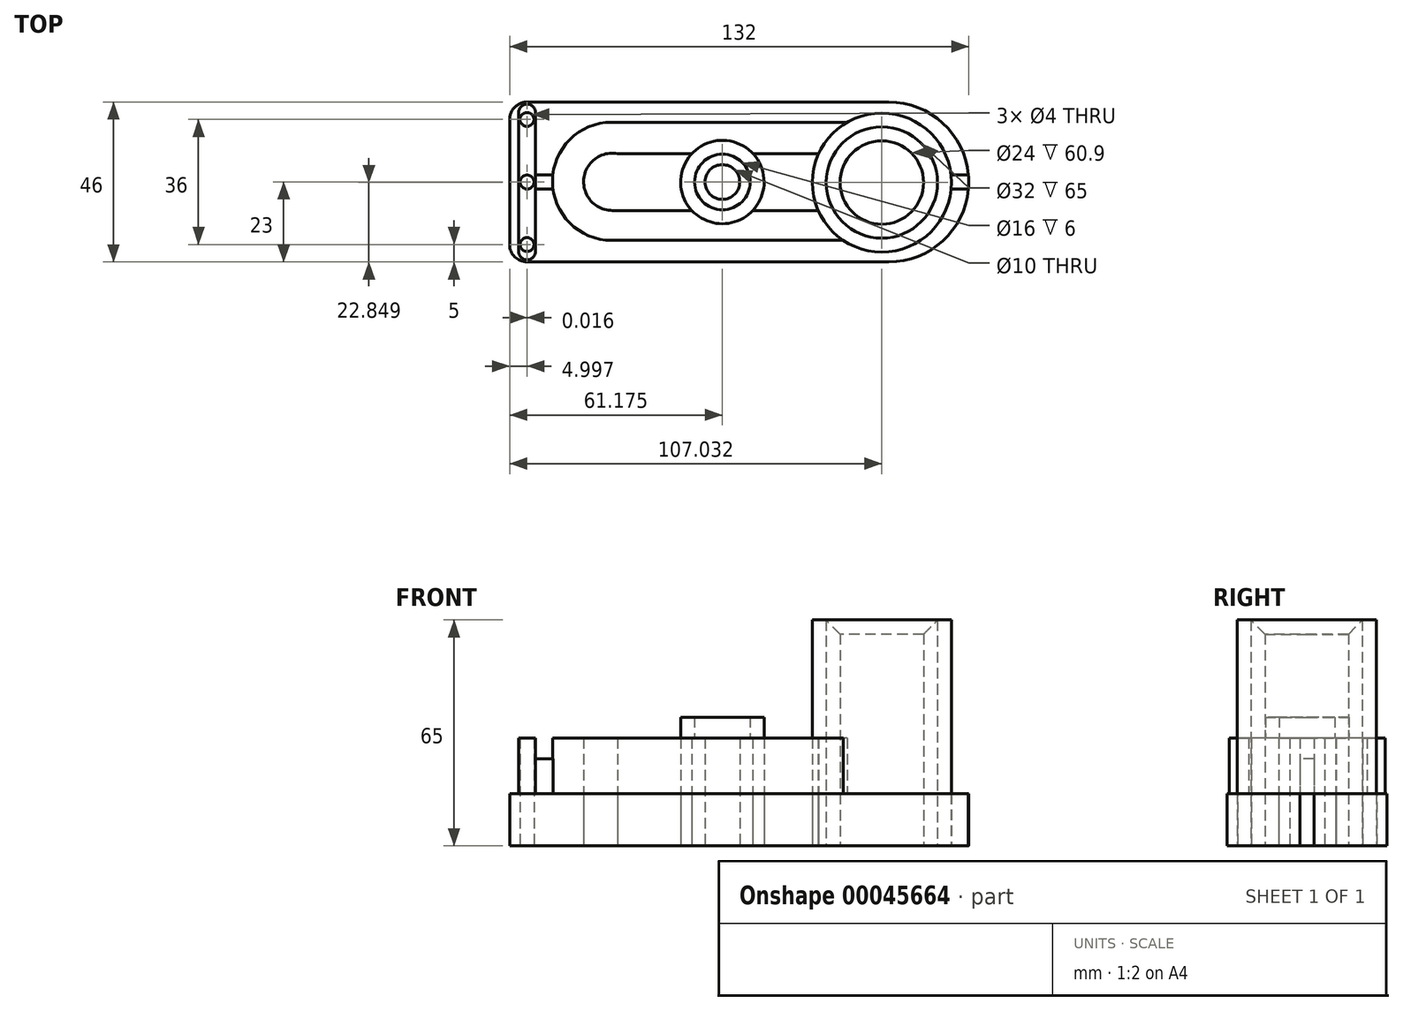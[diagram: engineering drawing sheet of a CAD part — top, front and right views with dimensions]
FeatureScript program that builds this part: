
annotation { "Feature Type Name" : "Feature", "Feature Type Description" : "" }
export const myFeature = defineFeature(function(context is Context, id is Id, definition is map)
    precondition{}
    {
        {
            var Q0;
            Q0=qCreatedBy(makeId("Top.planeOp"),FACE);
            var sketch = newSketch(context, id + "F0", { "sketchPlane" : qUnion([Q0])});
            skLineSegment(sketch, "E0.rect.bottom", {"start": v(54.5, 23) * mm, "end": v(-49.5, 23) * mm});
            skLineSegment(sketch, "E0.rect.top", {"start": v(54.5, -23) * mm, "end": v(-49.5, -23) * mm});
            skLineSegment(sketch, "E0.rect.right", {"start": v(-54.5, 18) * mm, "end": v(-54.5, -18) * mm});
            skPoint(sketch, "E0.rect.middle", {"position": v(0, 0) * mm});
            skPoint(sketch, "E1.endSnap0", {"position": v(52.53, -0.15) * mm});
            skArc(sketch, "E2", {"start": v(54.5, -23) * mm, "mid": v(77.5, 0) * mm, "end": v(54.5, 23) * mm});
            skPoint(sketch, "E3.visualSharp", {"position": v(-54.5, 23) * mm});
            skArc(sketch, "E3.filletArc", {"start": v(-49.5, 23) * mm, "mid": v(-53.04, 21.54) * mm, "end": v(-54.5, 18) * mm});
            skPoint(sketch, "E4.visualSharp", {"position": v(-54.5, -23) * mm});
            skArc(sketch, "E4.filletArc", {"start": v(-54.5, -18) * mm, "mid": v(-53.03, -21.54) * mm, "end": v(-49.5, -23) * mm});
            skCircle(sketch, "E5", {"center": v(52.53, -0.15) * mm, "radius": 20 * mm});
            skCircle(sketch, "E6", {"center": v(52.53, -0.15) * mm, "radius": 16 * mm});
            skCircle(sketch, "E7", {"center": v(52.53, -0.15) * mm, "radius": 12 * mm});
            skLineSegment(sketch, "E8", {"start": v(42.6, 17.2) * mm, "end": v(-25.17, 17.2) * mm});
            skLineSegment(sketch, "E9", {"start": v(41.44, -16.8) * mm, "end": v(-25.17, -16.8) * mm});
            skArc(sketch, "E10", {"start": v(-25.17, 17.2) * mm, "mid": v(-42.17, 0.2) * mm, "end": v(-25.17, -16.8) * mm});
            skCircle(sketch, "E11", {"center": v(6.68, 0) * mm, "radius": 12 * mm});
            skCircle(sketch, "E12", {"center": v(6.68, 0) * mm, "radius": 8 * mm});
            skCircle(sketch, "E13", {"center": v(6.68, 0) * mm, "radius": 5 * mm});
            skLineSegment(sketch, "E14", {"start": v(34.35, 8.18) * mm, "end": v(15.45, 8.18) * mm});
            skLineSegment(sketch, "E15", {"start": v(34.22, -8.18) * mm, "end": v(15.45, -8.18) * mm});
            skArc(sketch, "E16", {"start": v(-23.5, 8.18) * mm, "mid": v(-33.18, 0.8) * mm, "end": v(-24.96, -8.18) * mm});
            skLineSegment(sketch, "E17.trimOffspring", {"start": v(-2.1, 8.18) * mm, "end": v(-23.5, 8.18) * mm});
            skLineSegment(sketch, "E18.trimOffspring", {"start": v(-2.1, -8.18) * mm, "end": v(-24.96, -8.18) * mm});
            skLineSegment(sketch, "E19.rect.left", {"start": v(-47.06, 20) * mm, "end": v(-47.08, -20) * mm});
            skLineSegment(sketch, "E19.rect.right", {"start": v(-51.9, 20) * mm, "end": v(-51.9, -20) * mm});
            skPoint(sketch, "E19.rect.middle", {"position": v(-49.49, 0) * mm});
            skArc(sketch, "E20", {"start": v(-47.06, 20) * mm, "mid": v(-49.48, 22.41) * mm, "end": v(-51.9, 20) * mm});
            skArc(sketch, "E21", {"start": v(-51.9, -20) * mm, "mid": v(-49.5, -22.41) * mm, "end": v(-47.08, -20) * mm});
            skCircle(sketch, "E22", {"center": v(-49.49, 0) * mm, "radius": 2 * mm});
            skCircle(sketch, "E23", {"center": v(-49.5, 18) * mm, "radius": 2 * mm});
            skCircle(sketch, "E24", {"center": v(-49.5, -18) * mm, "radius": 2 * mm});
            skLineSegment(sketch, "E25", {"start": v(-47.07, 2) * mm, "end": v(-42.07, 2) * mm});
            skLineSegment(sketch, "E26", {"start": v(-47.07, -2) * mm, "end": v(-42.02, -2) * mm});
            skPoint(sketch, "E27.orphan", {"position": v(-49.49, 2) * mm});
            skPoint(sketch, "E28.orphan", {"position": v(-49.49, -2) * mm});
            skLineSegment(sketch, "E29", {"start": v(72.42, 2) * mm, "end": v(77.42, 2) * mm});
            skLineSegment(sketch, "E30", {"start": v(77.41, -2.05) * mm, "end": v(72.44, -2.05) * mm});
            skSolve(sketch);
        }
        {
            var Q0;
            {var subQ13=sQuery(id+"F0.wireOp",EDGE,"E0.rect.bottom");Q0=makeQuery(id+"F0.imprint","IMPRINT",FACE,{"disambiguationData":[TD([[makeQuery(id+"F0.imprint","IMPRINT",EDGE,{"derivedFrom":subQ13}),1.0]])]});}
            var Q1;
            {var subQ1=sQuery(id+"F0.wireOp",EDGE,"841581c3-ffe9-4fb2-872b-1de27e73801d");Q1=makeQuery(id+"F0.imprint","IMPRINT",FACE,{"disambiguationData":[TD([[makeQuery(id+"F0.imprint","IMPRINT",EDGE,{"derivedFrom":subQ1}),-1.0]])]});}
            extrude(context, id + "F1", {"entities" : qUnion([Q0, Q1]), "depth" : 15 * mm});
        }
        {
            var Q0;
            Q0=makeQuery(id+"F0.imprint","IMPRINT",FACE,{"disambiguationData":[TD([[makeQuery(id+"F0.imprint","IMPRINT",EDGE,{"derivedFrom":sQuery(id+"F0.wireOp",EDGE,"E19.rect.right")}),1.0]])]});
            extrude(context, id + "F2", {"entities" : qUnion([Q0]), "operationType" : NewBodyOperationType.ADD, "depth" : 31 * mm});
        }
        {
            var Q0;
            {var subQ1=sQuery(id+"F0.wireOp",EDGE,"E25");Q0=makeQuery(id+"F0.imprint","IMPRINT",FACE,{"disambiguationData":[TD([[makeQuery(id+"F0.imprint","IMPRINT",EDGE,{"derivedFrom":subQ1}),-1.0]])]});}
            extrude(context, id + "F3", {"entities" : qUnion([Q0]), "operationType" : NewBodyOperationType.ADD, "depth" : 25 * mm});
        }
        {
            var Q0;
            {var subQ4=sQuery(id+"F0.wireOp",EDGE,"E8");Q0=makeQuery(id+"F0.imprint","IMPRINT",FACE,{"disambiguationData":[TD([[makeQuery(id+"F0.imprint","IMPRINT",EDGE,{"derivedFrom":subQ4}),1.0]])]});}
            extrude(context, id + "F4", {"entities" : qUnion([Q0]), "operationType" : NewBodyOperationType.ADD, "depth" : 31 * mm});
        }
        {
            var Q0;
            Q0=makeQuery(id+"F0.imprint","IMPRINT",FACE,{"disambiguationData":[TD([[makeQuery(id+"F0.imprint","IMPRINT",EDGE,{"derivedFrom":sQuery(id+"F0.wireOp",EDGE,"E12")}),-1.0]])]});
            extrude(context, id + "F5", {"entities" : qUnion([Q0]), "operationType" : NewBodyOperationType.ADD, "depth" : 37 * mm});
        }
        {
            var Q0;
            Q0=makeQuery(id+"F0.imprint","IMPRINT",FACE,{"disambiguationData":[TD([[makeQuery(id+"F0.imprint","IMPRINT",EDGE,{"derivedFrom":sQuery(id+"F0.wireOp",EDGE,"E12")}),1.0]])]});
            extrude(context, id + "F6", {"entities" : qUnion([Q0]), "operationType" : NewBodyOperationType.ADD, "depth" : 31 * mm});
        }
        {
            var Q0;
            Q0=makeQuery(id+"F0.imprint","IMPRINT",FACE,{"disambiguationData":[TD([[makeQuery(id+"F0.imprint","IMPRINT",EDGE,{"derivedFrom":sQuery(id+"F0.wireOp",EDGE,"E6")}),1.0]])]});
            extrude(context, id + "F7", {"entities" : qUnion([Q0]), "depth" : 65 * mm});
        }
        {
            var Q0;
            Q0=makeQuery(id+"F0.imprint","IMPRINT",FACE,{"disambiguationData":[TD([[makeQuery(id+"F0.imprint","IMPRINT",EDGE,{"derivedFrom":sQuery(id+"F0.wireOp",EDGE,"E6")}),-1.0]])]});
            extrude(context, id + "F8", {"entities" : qUnion([Q0]), "depth" : 65 * mm});
        }
        {
            var Q0;
            Q0=makeQuery(id+"F7.opExtrude","CAP_EDGE",EDGE,{"disambiguationData":[OSD([sQuery(id+"F0.wireOp",EDGE,"E7")])],"isStart":false});
            chamfer(context, id + "F9", {"entities" : qUnion([Q0]), "width" : 4.1 * mm, "tangentPropagation" : true});
        }
        {
            var Q0;
            Q0=makeQuery(id+"F0.imprint","IMPRINT",FACE,{"disambiguationData":[TD([[makeQuery(id+"F0.imprint","IMPRINT",EDGE,{"derivedFrom":sQuery(id+"F0.wireOp",EDGE,"E16")}),1.0]])]});
            var Q1;
            {var subQ1=sQuery(id+"F0.wireOp",EDGE,"E14");Q1=makeQuery(id+"F0.imprint","IMPRINT",FACE,{"disambiguationData":[TD([[makeQuery(id+"F0.imprint","IMPRINT",EDGE,{"derivedFrom":subQ1}),1.0]])]});}
            extrude(context, id + "F10", {"entities" : qUnion([Q0, Q1]), "depth" : 15 * mm});
        }
        {
            var Q0;
            {var subQ1=sQuery(id+"F0.wireOp",EDGE,"E29");Q0=makeQuery(id+"F0.imprint","IMPRINT",FACE,{"disambiguationData":[TD([[makeQuery(id+"F0.imprint","IMPRINT",EDGE,{"derivedFrom":subQ1}),-1.0]])]});}
            extrude(context, id + "F11", {"entities" : qUnion([Q0]), "depth" : 15 * mm});
        }
    });
